# Revit family: EBRME9-R4X055_15xx-OS
name_source: partatom
category: Leuchten
units: mm (PartAtom-declared; Revit-internal decimal feet)

## family parameters
Basisbauteil = Fläche
Beim Laden mit Abzugskörper schneiden = Nein
Bemaßung runder Anschluss = Durchmesser verwenden
Gemeinsam genutzt = Nein
Lichtquelle = Ja
OmniClass-Nummer = 23.80.70.11
OmniClass-Titel = Luminaries for Internal Lighting
Raumberechnungspunkt = Nein
Teiletyp = Normal

## types (2) — shared parameters
Baugruppenkennzeichen = D5020200
Datei für fotometrisches Netz = EBRME9-R4x-OS.IES
Emissionsform beim Rendern sichtbar = Nein
Farbfilter = 16777215
Farbtemperaturverschiebung bei Dämpfen der Lampe = <Keine Auswahl>
Hersteller = RIDI Leuchten GmbH
Lampe = LED
Neigungswinkel = 90.00°
Scheinlast = 60 VA
URL = www.ridi.de
Von Breite des Rechtecks ausssenden = 575 mm
Von Länge des Rechtecks aussenden = 575 mm
brand = RIDI
conformity mark = CE
electrical safety class = 1
height = 95 mm
ingress protection (IP) code = IP20/IP40
length = 597 mm
nominal frequency = 50-60Hz
nominal voltage = 230
rated input power = 60
voltage type (AC, DC, UC) = AC
weight = 2.95
width = 597 mm
zero-valued in all types: Vorgabe-Ansicht

## per-type parameters (varying)
| type | Modell |
| EBRME9-R4X055/15ND-OS | 0850094 |
| EBRME9-R4X055/15DA-OS | 0860094 |

note: column(s) folded — value = type name in every type: product name
